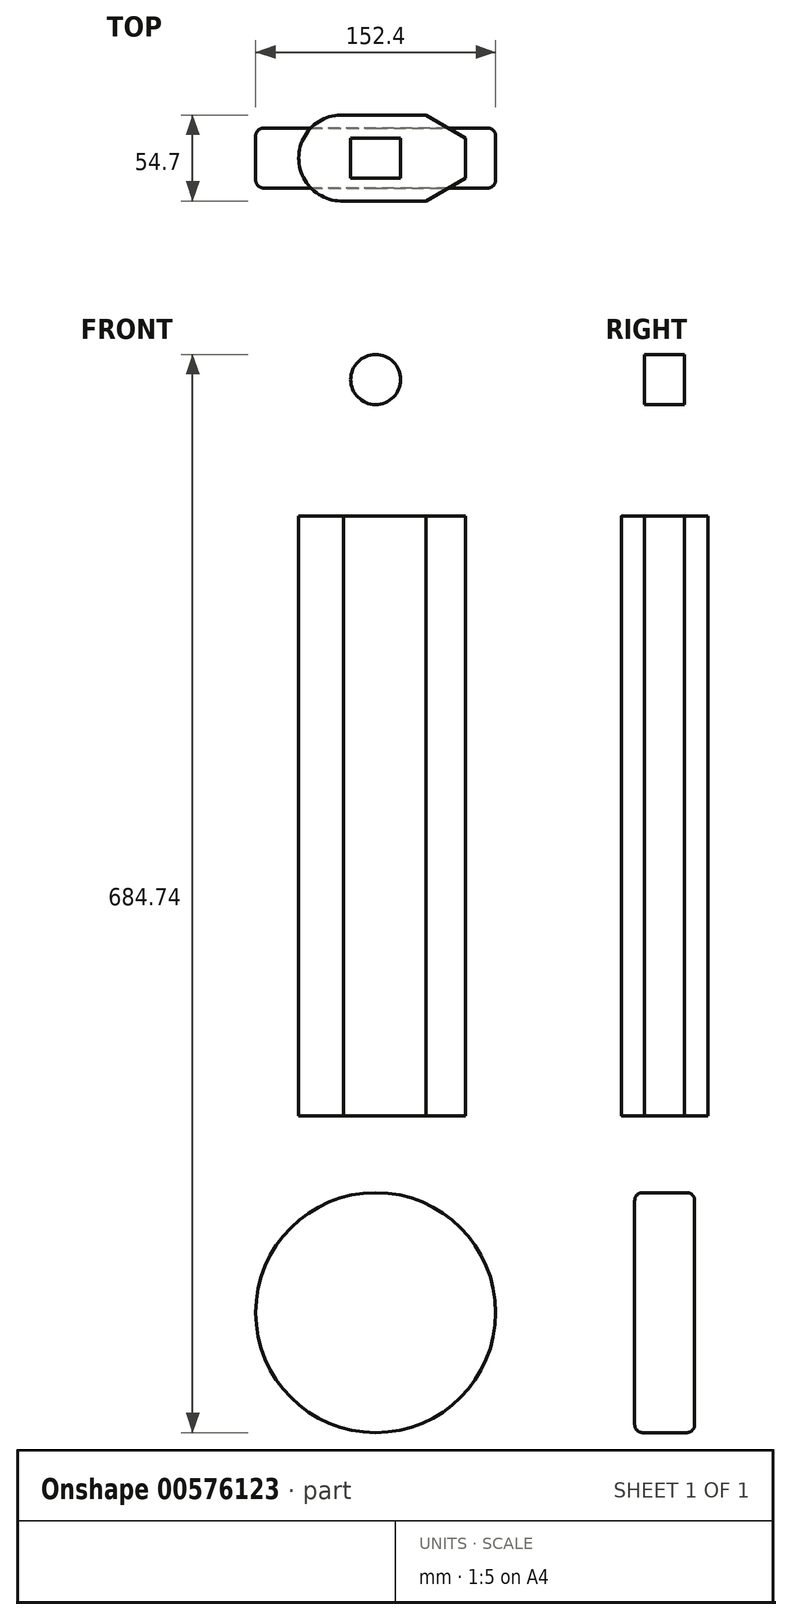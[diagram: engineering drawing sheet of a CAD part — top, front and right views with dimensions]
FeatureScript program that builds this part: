
annotation { "Feature Type Name" : "Feature", "Feature Type Description" : "" }
export const myFeature = defineFeature(function(context is Context, id is Id, definition is map)
    precondition{}
    {
        {
            var Q0;
            Q0=qCreatedBy(makeId("Front.planeOp"),FACE);
            var sketch = newSketch(context, id + "F0", { "sketchPlane" : qUnion([Q0])});
            skLineSegment(sketch, "E0.bottom", {"start": v(-19.05, 212.03) * mm, "end": v(57.15, 212.03) * mm});
            skLineSegment(sketch, "E0.top", {"start": v(-19.05, -168.97) * mm, "end": v(57.15, -168.97) * mm});
            skLineSegment(sketch, "E0.left", {"start": v(-19.05, 212.03) * mm, "end": v(-19.05, -168.97) * mm});
            skLineSegment(sketch, "E0.right", {"start": v(57.15, 212.03) * mm, "end": v(57.15, -168.97) * mm});
            skCircle(sketch, "E1", {"center": v(0, 298.62) * mm, "radius": 15.88 * mm});
            skCircle(sketch, "E2", {"center": v(0, -294.04) * mm, "radius": 76.2 * mm});
            skLineSegment(sketch, "E3.bottom", {"start": v(0, -168.97) * mm, "end": v(17.08, -168.97) * mm});
            skLineSegment(sketch, "E4.bottom", {"start": v(-11.02, -168.97) * mm, "end": v(20.2, -168.97) * mm});
            skLineSegment(sketch, "E4.top", {"start": v(-11.02, -232.36) * mm, "end": v(20.2, -232.36) * mm});
            skLineSegment(sketch, "E4.left", {"start": v(-11.02, -168.97) * mm, "end": v(-11.02, -232.36) * mm});
            skLineSegment(sketch, "E4.right", {"start": v(20.2, -168.97) * mm, "end": v(20.2, -232.36) * mm});
            skSolve(sketch);
        }
        {
            var Q0;
            Q0=makeQuery(id+"F0.imprint","IMPRINT",FACE,{"disambiguationData":[TD([[makeQuery(id+"F0.imprint","IMPRINT",EDGE,{"derivedFrom":sQuery(id+"F0.wireOp",EDGE,"E0.bottom")}),-1.0]])]});
            var Q1;
            {var subQ1=sQuery(id+"F0.wireOp",EDGE,"E4.bottom");var subQ5=makeQuery(id+"F0.imprint","IMPRINT",VERTEX,{"disambiguationData":[OD(0.0)],"derivedFrom":subQ1});Q1=makeQuery(id+"F0.imprint","IMPRINT",FACE,{"disambiguationData":[TD([[makeQuery(id+"F0.imprint","IMPRINT",EDGE,{"disambiguationData":[TD([[subQ5,-1.0]])],"derivedFrom":subQ1}),-1.0]])]});}
            extrude(context, id + "F1", {"entities" : qUnion([Q0, Q1]), "endBound" : BoundingType.SYMMETRIC, "depth" : 25.4 * mm, "offsetDistance" : 25.4 * mm});
        }
        {
            var Q0;
            Q0=makeQuery(id+"F0.imprint","IMPRINT",FACE,{"disambiguationData":[TD([[makeQuery(id+"F0.imprint","IMPRINT",EDGE,{"derivedFrom":sQuery(id+"F0.wireOp",EDGE,"E1")}),1.0]])]});
            extrude(context, id + "F2", {"entities" : qUnion([Q0]), "endBound" : BoundingType.SYMMETRIC, "depth" : 25.4 * mm, "offsetDistance" : 25.4 * mm});
        }
        {
            var Q0;
            {var subQ5=sQuery(id+"F0.wireOp",EDGE,"E4.top");Q0=makeQuery(id+"F0.imprint","IMPRINT",FACE,{"disambiguationData":[TD([[makeQuery(id+"F0.imprint","IMPRINT",EDGE,{"derivedFrom":subQ5}),-1.0]])]});}
            var Q1;
            {var subQ5=sQuery(id+"F0.wireOp",EDGE,"E4.top");Q1=makeQuery(id+"F0.imprint","IMPRINT",FACE,{"disambiguationData":[TD([[makeQuery(id+"F0.imprint","IMPRINT",EDGE,{"derivedFrom":subQ5}),1.0]])]});}
            extrude(context, id + "F3", {"entities" : qUnion([Q0, Q1]), "operationType" : NewBodyOperationType.ADD, "endBound" : BoundingType.SYMMETRIC, "depth" : 38.1 * mm, "offsetDistance" : 25.4 * mm});
        }
        {
            var Q0;
            {var subQ0=sQuery(id+"F0.wireOp",EDGE,"E0.top");Q0=makeQuery(id+"F1.opExtrude","SWEPT_FACE",FACE,{"disambiguationData":[OSD([subQ0]),TDD([makeQuery(id+"F0.imprint","IMPRINT",EDGE,{"disambiguationData":[TD([[makeQuery(id+"F0.imprint","INTERSECT",VERTEX,{"derivedFrom":[subQ0,sQuery(id+"F0.wireOp",EDGE,"E0.right")]}),1.0]])],"derivedFrom":subQ0})])]});}
            var sketch = newSketch(context, id + "F4", { "sketchPlane" : qUnion([Q0])});
            skArc(sketch, "E5", {"start": v(-20.38, 27.33) * mm, "mid": v(-48.9, 0) * mm, "end": v(-20.38, -27.33) * mm});
            skLineSegment(sketch, "E6", {"start": v(-20.38, 27.33) * mm, "end": v(31.81, 27.33) * mm});
            skLineSegment(sketch, "E7", {"start": v(31.81, 27.33) * mm, "end": v(57.15, 12.7) * mm});
            skLineSegment(sketch, "E8", {"start": v(57.15, 12.7) * mm, "end": v(57.15, 0) * mm});
            skLineSegment(sketch, "E9.MirrorCS", {"start": v(-20.38, -27.33) * mm, "end": v(31.81, -27.33) * mm});
            skLineSegment(sketch, "E10.MirrorCS", {"start": v(31.81, -27.33) * mm, "end": v(57.15, -12.7) * mm});
            skLineSegment(sketch, "E11.MirrorCS", {"start": v(57.15, -12.7) * mm, "end": v(57.15, 0) * mm});
            skSolve(sketch);
        }
        {
            var Q0;
            Q0=makeQuery(id+"F4.imprint","IMPRINT",FACE,{"disambiguationData":[TD([[makeQuery(id+"F4.imprint","IMPRINT",EDGE,{"derivedFrom":sQuery(id+"F4.wireOp",EDGE,"E5")}),1.0]])]});
            var Q1;
            Q1=makeQuery(id+"F4.imprint","IMPRINT",FACE,{"disambiguationData":[TD([[makeQuery(id+"F4.imprint","IMPRINT",EDGE,{"derivedFrom":sQuery(id+"F4.wireOp",EDGE,"E8")}),-1.0]])]});
            var Q2;
            Q2=makeQuery(id+"F1.opExtrude","SWEPT_FACE",FACE,{"disambiguationData":[OSD([sQuery(id+"F0.wireOp",EDGE,"E0.bottom")])]});
            extrude(context, id + "F5", {"entities" : qUnion([Q0, Q1]), "operationType" : NewBodyOperationType.ADD, "endBound" : BoundingType.UP_TO_SURFACE, "oppositeDirection" : true, "depth" : 25.4 * mm, "endBoundEntityFace" : qUnion([Q2]), "offsetDistance" : 25.4 * mm});
        }
        {
            var Q0;
            Q0=makeQuery(id+"F3.opExtrude","CAP_EDGE",EDGE,{"disambiguationData":[OSD([sQuery(id+"F0.wireOp",EDGE,"E2")])],"isStart":false});
            var Q1;
            Q1=makeQuery(id+"F3.opExtrude","CAP_EDGE",EDGE,{"disambiguationData":[OSD([sQuery(id+"F0.wireOp",EDGE,"E2")])],"isStart":true});
            fillet(context, id + "F6", {"entities" : qUnion([Q0, Q1]), "radius" : 5.08 * mm, "tangentPropagation" : true, "allowEdgeOverflow" : false});
        }
    });
